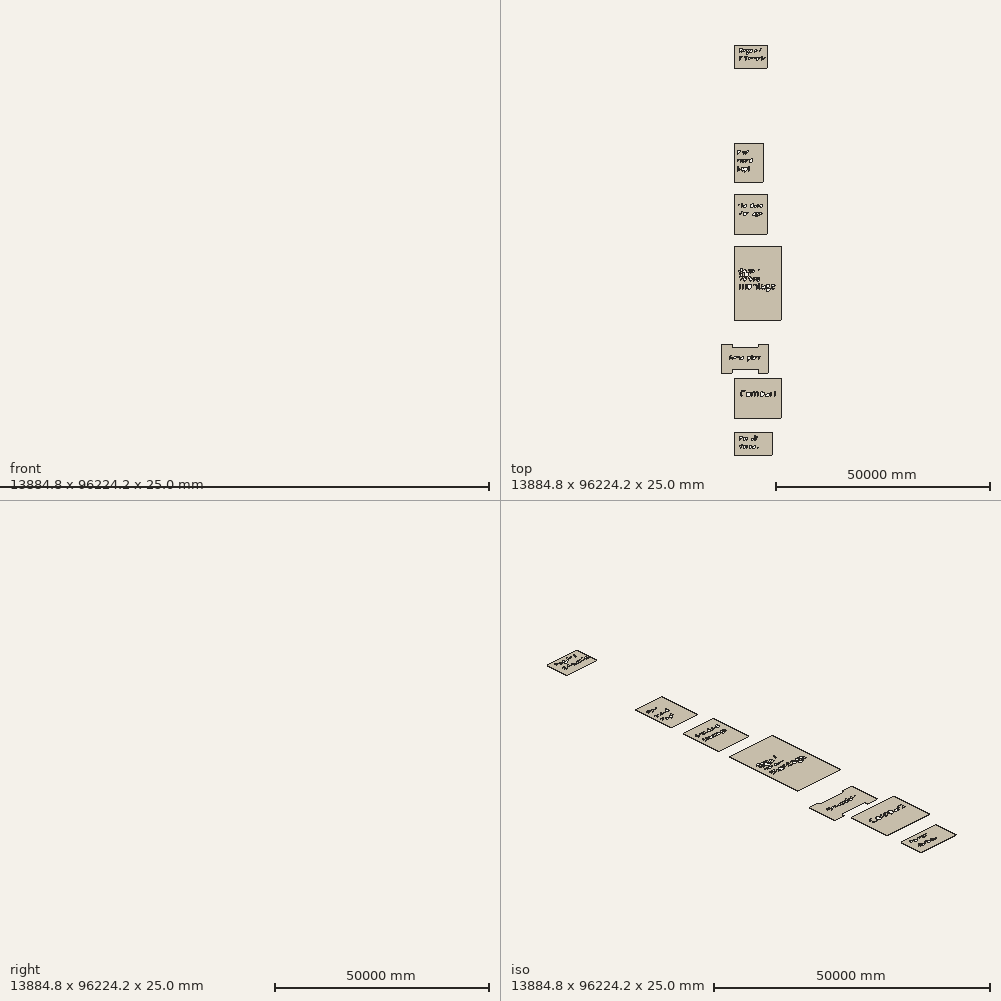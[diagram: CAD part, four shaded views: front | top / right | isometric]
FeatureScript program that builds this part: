
annotation { "Feature Type Name" : "Feature", "Feature Type Description" : "" }
export const myFeature = defineFeature(function(context is Context, id is Id, definition is map)
    precondition{}
    {
        {
            var Q0;
            Q0=qCreatedBy(makeId("Top.planeOp"),FACE);
            var sketch = newSketch(context, id + "F0", { "sketchPlane" : qUnion([Q0])});
            skLineSegment(sketch, "E0.bottom", {"start": v(0, 0) * mm, "end": v(9000, 0) * mm});
            skLineSegment(sketch, "E0.top", {"start": v(0, 5300) * mm, "end": v(9000, 5300) * mm});
            skLineSegment(sketch, "E0.left", {"start": v(0, 0) * mm, "end": v(0, 5300) * mm});
            skLineSegment(sketch, "E0.right", {"start": v(9000, 0) * mm, "end": v(9000, 5300) * mm});
            skText(sketch, "E1", { "text": "Portal / \nVorbau\n", "fontName": "OpenSans-Regular.ttf"});
            skLineSegment(sketch, "E2", {"start": v(0, 0) * mm, "end": v(0, 105978.46) * mm, "construction": true});
            skLineSegment(sketch, "E3.bottom", {"start": v(0, 8738.85) * mm, "end": v(11000, 8738.85) * mm});
            skLineSegment(sketch, "E3.top", {"start": v(0, 17988.85) * mm, "end": v(11000, 17988.85) * mm});
            skLineSegment(sketch, "E3.left", {"start": v(0, 8738.85) * mm, "end": v(0, 17988.85) * mm});
            skLineSegment(sketch, "E3.right", {"start": v(11000, 8738.85) * mm, "end": v(11000, 17988.85) * mm});
            skText(sketch, "E4", { "text": "Compact", "fontName": "OpenSans-Regular.ttf"});
            skLineSegment(sketch, "E5.bottom", {"start": v(2615.24, 20121.73) * mm, "end": v(5615.24, 20121.73) * mm});
            skLineSegment(sketch, "E5.top", {"start": v(2615.24, 25421.73) * mm, "end": v(5615.24, 25421.73) * mm});
            skLineSegment(sketch, "E5.left", {"start": v(0, 20121.73) * mm, "end": v(0, 25421.73) * mm});
            skText(sketch, "E6", { "text": "Genauplatz", "fontName": "OpenSans-Regular.ttf"});
            skLineSegment(sketch, "E7", {"start": v(2615.24, 20121.73) * mm, "end": v(2615.24, 29543.85) * mm, "construction": true});
            skLineSegment(sketch, "E8.bottom", {"start": v(5615.24, 26028.16) * mm, "end": v(8115.24, 26028.16) * mm});
            skLineSegment(sketch, "E8.top", {"start": v(5615.24, 19327.66) * mm, "end": v(8115.24, 19327.66) * mm});
            skLineSegment(sketch, "E8.left", {"start": v(5615.24, 26028.16) * mm, "end": v(5615.24, 25421.73) * mm});
            skLineSegment(sketch, "E8.right", {"start": v(8115.24, 26028.16) * mm, "end": v(8115.24, 19327.66) * mm});
            skLineSegment(sketch, "E9.trimOffspring", {"start": v(5615.24, 20121.73) * mm, "end": v(5615.24, 19327.66) * mm});
            skPoint(sketch, "E10.orphan", {"position": v(5230.49, 20121.73) * mm});
            skLineSegment(sketch, "E11.MirrorCS", {"start": v(-384.76, 26028.16) * mm, "end": v(-384.76, 25421.73) * mm});
            skLineSegment(sketch, "E12.MirrorCS", {"start": v(-384.76, 20121.73) * mm, "end": v(-384.76, 19327.66) * mm});
            skLineSegment(sketch, "E13.MirrorCS", {"start": v(2615.24, 25421.73) * mm, "end": v(-384.76, 25421.73) * mm});
            skLineSegment(sketch, "E14.MirrorCS", {"start": v(-384.76, 19327.66) * mm, "end": v(-2884.76, 19327.66) * mm});
            skLineSegment(sketch, "E15.MirrorCS", {"start": v(-2884.76, 26028.16) * mm, "end": v(-2884.76, 19327.66) * mm});
            skLineSegment(sketch, "E16.MirrorCS", {"start": v(-384.76, 26028.16) * mm, "end": v(-2884.76, 26028.16) * mm});
            skLineSegment(sketch, "E17.MirrorCS", {"start": v(2615.24, 20121.73) * mm, "end": v(-384.76, 20121.73) * mm});
            skPoint(sketch, "E18.MirrorP", {"position": v(0, 20121.73) * mm});
            skLineSegment(sketch, "E19.bottom", {"start": v(0, 31660.35) * mm, "end": v(11000, 31660.35) * mm});
            skLineSegment(sketch, "E19.top", {"start": v(0, 49160.35) * mm, "end": v(11000, 49160.35) * mm});
            skLineSegment(sketch, "E19.left", {"start": v(0, 31660.35) * mm, "end": v(0, 49160.35) * mm});
            skLineSegment(sketch, "E19.right", {"start": v(11000, 31660.35) * mm, "end": v(11000, 49160.35) * mm});
            skText(sketch, "E20", { "text": "Vor-\nmontage\n", "fontName": "OpenSans-Regular.ttf"});
            skLineSegment(sketch, "E21.bottom", {"start": v(0, 51940.27) * mm, "end": v(7800, 51940.27) * mm});
            skLineSegment(sketch, "E21.top", {"start": v(0, 61190.27) * mm, "end": v(7800, 61190.27) * mm});
            skLineSegment(sketch, "E21.left", {"start": v(0, 51940.27) * mm, "end": v(0, 61190.27) * mm});
            skLineSegment(sketch, "E21.right", {"start": v(7800, 51940.27) * mm, "end": v(7800, 61190.27) * mm});
            skText(sketch, "E22", { "text": "Standard\nMontage", "fontName": "OpenSans-Regular.ttf"});
            skLineSegment(sketch, "E23.bottom", {"start": v(0, 64090.89) * mm, "end": v(6800, 64090.89) * mm});
            skLineSegment(sketch, "E23.top", {"start": v(0, 73340.89) * mm, "end": v(6800, 73340.89) * mm});
            skLineSegment(sketch, "E23.left", {"start": v(0, 64090.89) * mm, "end": v(0, 73340.89) * mm});
            skLineSegment(sketch, "E23.right", {"start": v(6800, 64090.89) * mm, "end": v(6800, 73340.89) * mm});
            skText(sketch, "E24", { "text": "Prüf-\nstand \nKopf", "fontName": "OpenSans-Regular.ttf"});
            skLineSegment(sketch, "E25.bottom", {"start": v(0, 90924.17) * mm, "end": v(7800, 90924.17) * mm});
            skLineSegment(sketch, "E25.top", {"start": v(0, 96224.17) * mm, "end": v(7800, 96224.17) * mm});
            skLineSegment(sketch, "E25.left", {"start": v(0, 90924.17) * mm, "end": v(0, 96224.17) * mm});
            skLineSegment(sketch, "E25.right", {"start": v(7800, 90924.17) * mm, "end": v(7800, 96224.17) * mm});
            skText(sketch, "E26", { "text": "Regale /\nE-Technik", "fontName": "OpenSans-Regular.ttf"});
            skText(sketch, "E27", { "text": "Portal/\nVorbau", "fontName": "OpenSans-Regular.ttf"});
            const initialGuessF0  = {"E1": [1.26928, 42.8333, 1, 0, 1], "E4": [1.39647, 13.7739, 1, 0, 1.5], "E6": [-1.16452, 22.4587, 1, 0, 1], "E20": [1.04947, 41.9069, 1, 0, 1.5], "E22": [0.8676, 58.2045, 1, 0, 1], "E24": [0.70105, 70.54244, 1, 0, 1], "E26": [1.18194, 94.50346, 1, 0, 1], "E27": [1.17226, 3.523, 1, 0, 1]};
            skSetInitialGuess(sketch, initialGuessF0);
            skSolve(sketch);
        }
        {
            var Q0;
            Q0=makeQuery(id+"F0.imprint","IMPRINT",FACE,{"disambiguationData":[TD([[makeQuery(id+"F0.imprint","IMPRINT",EDGE,{"derivedFrom":sQuery(id+"F0.wireOp",EDGE,"E0.bottom")}),1.0]])]});
            extrude(context, id + "F1", {"entities" : qUnion([Q0]), "depth" : 25 * mm, "offsetDistance" : 25 * mm});
        }
        {
            var Q0;
            Q0=makeQuery(id+"F0.imprint","IMPRINT",FACE,{"disambiguationData":[TD([[makeQuery(id+"F0.imprint","IMPRINT",EDGE,{"derivedFrom":sQuery(id+"F0.wireOp",EDGE,"E3.bottom")}),1.0]])]});
            extrude(context, id + "F2", {"entities" : qUnion([Q0]), "depth" : 25 * mm, "offsetDistance" : 25 * mm});
        }
        {
            var Q0;
            Q0=makeQuery(id+"F0.imprint","IMPRINT",FACE,{"disambiguationData":[TD([[makeQuery(id+"F0.imprint","IMPRINT",EDGE,{"derivedFrom":sQuery(id+"F0.wireOp",EDGE,"E5.bottom")}),1.0]])]});
            var Q1;
            Q1=makeQuery(id+"F0.imprint","IMPRINT",FACE,{"disambiguationData":[TD([[makeQuery(id+"F0.imprint","IMPRINT",EDGE,{"derivedFrom":sQuery(id+"F0.wireOp",EDGE,"E6.sketch_text.stroke-0")}),1.0]])]});
            extrude(context, id + "F3", {"entities" : qUnion([Q0, Q1]), "depth" : 25 * mm, "offsetDistance" : 25 * mm});
        }
        {
            var Q0;
            Q0=makeQuery(id+"F0.imprint","IMPRINT",FACE,{"disambiguationData":[TD([[makeQuery(id+"F0.imprint","IMPRINT",EDGE,{"derivedFrom":sQuery(id+"F0.wireOp",EDGE,"E19.bottom")}),1.0]])]});
            extrude(context, id + "F4", {"entities" : qUnion([Q0]), "depth" : 25 * mm, "offsetDistance" : 25 * mm});
        }
        {
            var Q0;
            Q0=makeQuery(id+"F0.imprint","IMPRINT",FACE,{"disambiguationData":[TD([[makeQuery(id+"F0.imprint","IMPRINT",EDGE,{"derivedFrom":sQuery(id+"F0.wireOp",EDGE,"E21.bottom")}),1.0]])]});
            extrude(context, id + "F5", {"entities" : qUnion([Q0]), "depth" : 25 * mm, "offsetDistance" : 25 * mm});
        }
        {
            var Q0;
            Q0=makeQuery(id+"F0.imprint","IMPRINT",FACE,{"disambiguationData":[TD([[makeQuery(id+"F0.imprint","IMPRINT",EDGE,{"derivedFrom":sQuery(id+"F0.wireOp",EDGE,"E23.bottom")}),1.0]])]});
            extrude(context, id + "F6", {"entities" : qUnion([Q0]), "depth" : 25 * mm, "offsetDistance" : 25 * mm});
        }
        {
            var Q0;
            Q0=makeQuery(id+"F0.imprint","IMPRINT",FACE,{"disambiguationData":[TD([[makeQuery(id+"F0.imprint","IMPRINT",EDGE,{"derivedFrom":sQuery(id+"F0.wireOp",EDGE,"E25.bottom")}),1.0]])]});
            extrude(context, id + "F7", {"entities" : qUnion([Q0]), "depth" : 25 * mm, "offsetDistance" : 25 * mm});
        }
    });
